# Revit family: Haworth_BuzziCane_Sofas
name_source: partatom
category: Furniture
revit_build: Autodesk Revit 2018 (Build: 20170223_1515(x64)
units: mm (PartAtom-declared; Revit-internal decimal feet)

## family parameters
Always vertical = Yes
Cut with Voids When Loaded = No
OmniClass Number = 23.40.70.14.64.21
OmniClass Title = Systems Furniture
Room Calculation Point = No
Shared = No
Work Plane-Based = No

## types (2) — shared parameters
Actual Depth = 35.83 "
Actual Height = 32.68 "
Assembly Code = E2020200
Frame Offset = 3.93 "
Manufacturer = Haworth
Model = HCBZ-CNL
Revision Number = 1
Size = Verify Final Dim. w/ Haworth
URL = http://www.haworth.com
URL - Product = https://www.haworth.com
Warranty = http://www.haworth.com
Wood Finish = Haworth _ Wood _ Collection _ Ash Natural

## per-type parameters (varying)
| type | Actual Width | Description | Seat Offset | Three Seats | Two Seats |
| HCBZ-CNL2 - Two Seats | 78.35 " | Haworth BuzziCane Two Seats Sofa | 18.3 " | No | Yes |
| HCBZ-CNL3 - Three Seats | 105.51 " | Haworth BuzziCane - Three Seats Sofa | 33.65 " | Yes | No |

## geometry (parser evidence)
native form markers: Sweep x7
no freeform markers — native parametric forms only
